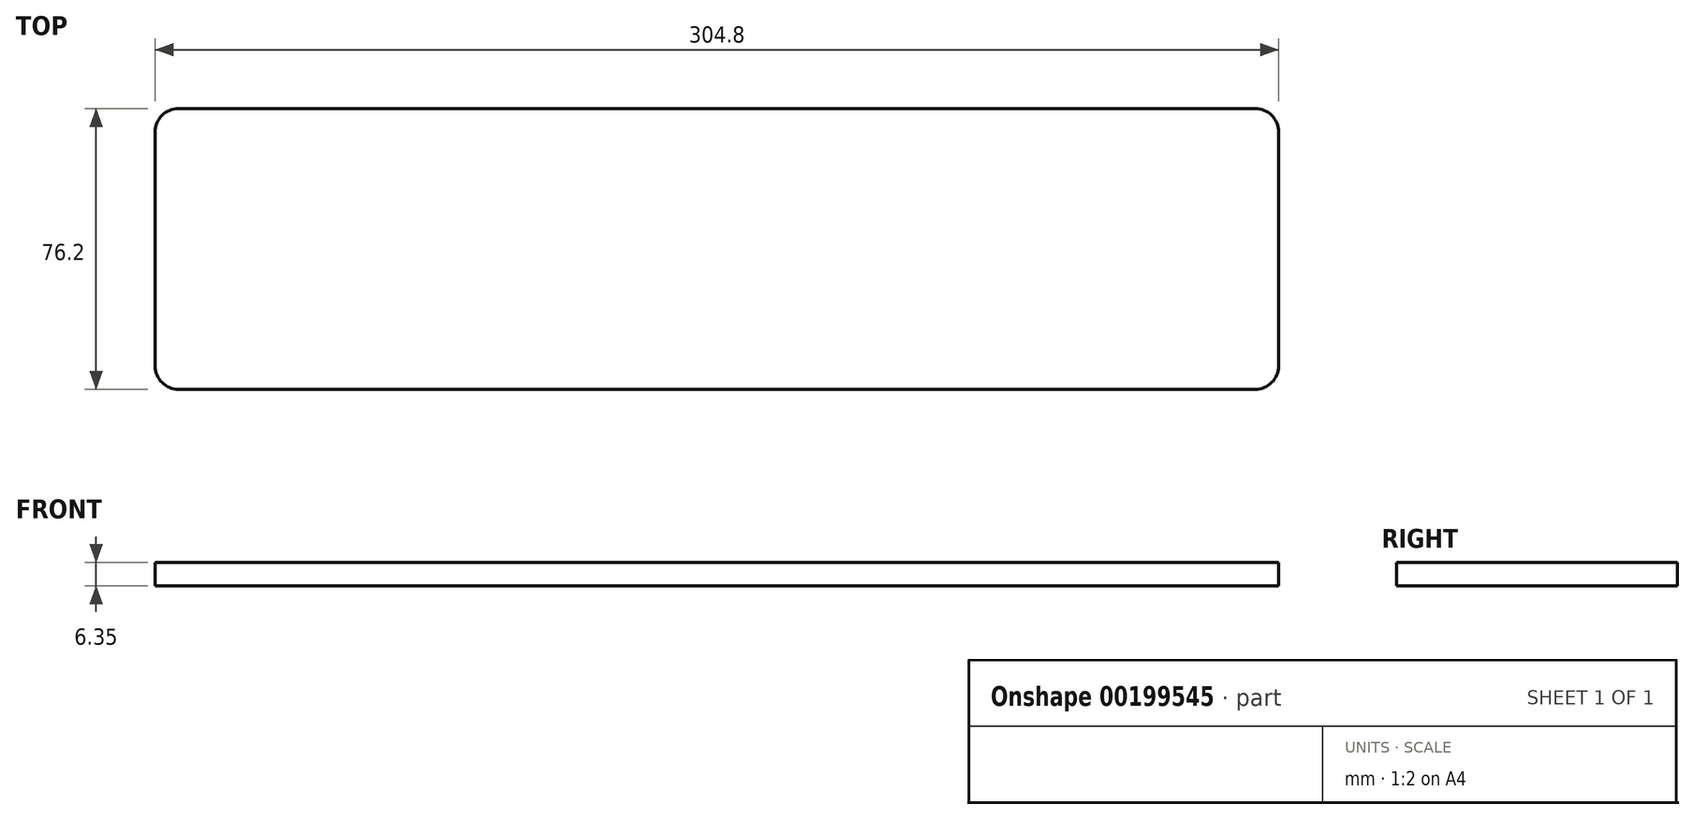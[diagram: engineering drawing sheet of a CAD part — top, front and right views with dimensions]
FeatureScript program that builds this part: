
annotation { "Feature Type Name" : "Feature", "Feature Type Description" : "" }
export const myFeature = defineFeature(function(context is Context, id is Id, definition is map)
    precondition{}
    {
        {
            var Q0;
            Q0=qCreatedBy(makeId("Top.planeOp"),FACE);
            var sketch = newSketch(context, id + "F1", { "sketchPlane" : qUnion([Q0])});
            skLineSegment(sketch, "E0.bottom", {"start": v(146.05, -38.1) * mm, "end": v(-146.05, -38.1) * mm});
            skLineSegment(sketch, "E0.top", {"start": v(146.05, 38.1) * mm, "end": v(-146.05, 38.1) * mm});
            skLineSegment(sketch, "E0.left", {"start": v(152.4, -31.75) * mm, "end": v(152.4, 31.75) * mm});
            skLineSegment(sketch, "E0.right", {"start": v(-152.4, -31.75) * mm, "end": v(-152.4, 31.75) * mm});
            skPoint(sketch, "E0.middle", {"position": v(0, 0) * mm});
            skPoint(sketch, "E1.visualSharp", {"position": v(-152.4, 38.1) * mm});
            skArc(sketch, "E1.filletArc", {"start": v(-146.05, 38.1) * mm, "mid": v(-150.54, 36.24) * mm, "end": v(-152.4, 31.75) * mm});
            skPoint(sketch, "E2.visualSharp", {"position": v(-152.4, -38.1) * mm});
            skArc(sketch, "E2.filletArc", {"start": v(-152.4, -31.75) * mm, "mid": v(-150.54, -36.24) * mm, "end": v(-146.05, -38.1) * mm});
            skPoint(sketch, "E3.visualSharp", {"position": v(152.4, -38.1) * mm});
            skArc(sketch, "E3.filletArc", {"start": v(146.05, -38.1) * mm, "mid": v(150.54, -36.24) * mm, "end": v(152.4, -31.75) * mm});
            skPoint(sketch, "E4.visualSharp", {"position": v(152.4, 38.1) * mm});
            skArc(sketch, "E4.filletArc", {"start": v(152.4, 31.75) * mm, "mid": v(150.54, 36.24) * mm, "end": v(146.05, 38.1) * mm});
            skSolve(sketch);
        }
        {
            var Q0;
            Q0=makeQuery(id+"F1.imprint","IMPRINT",FACE,{"disambiguationData":[TD([[makeQuery(id+"F1.imprint","IMPRINT",EDGE,{"derivedFrom":sQuery(id+"F1.wireOp",EDGE,"E0.bottom")}),-1.0]])]});
            extrude(context, id + "F2", {"entities" : qUnion([Q0]), "depth" : 6.35 * mm});
        }
    });
